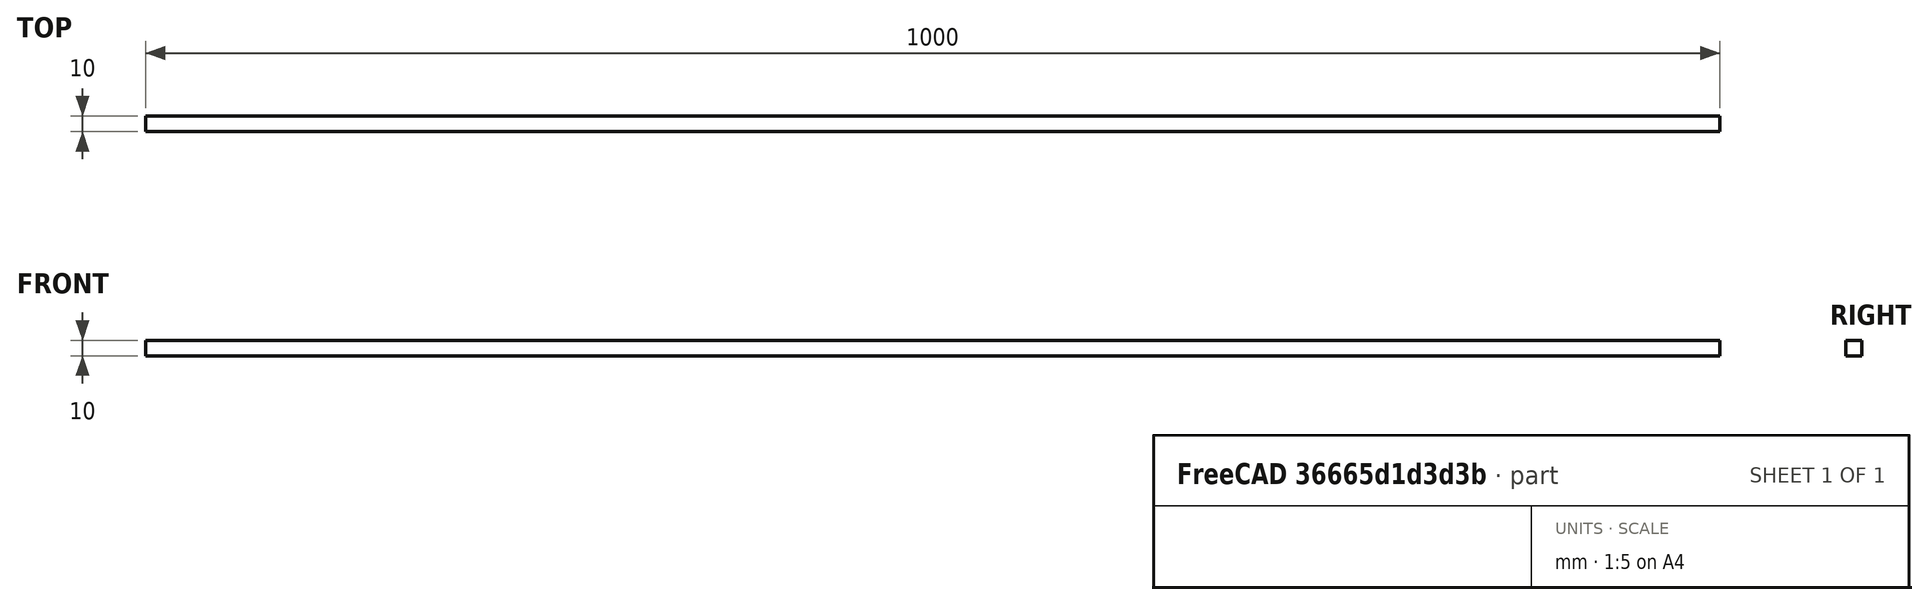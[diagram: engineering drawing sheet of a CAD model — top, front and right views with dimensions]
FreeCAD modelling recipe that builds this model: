
FCSTD DOCUMENT  (FreeCAD 0.21R33694 (Git))
Label: Elastica
License: All rights reserved
LicenseURL: http://en.wikipedia.org/wiki/All_rights_reserved
objects: Fem::FemMeshObjectPython×2, Part::Box×1, Fem::ConstraintForce×1, Fem::ConstraintFixed×1, App::MaterialObjectPython×1, Fem::FemSolverObjectPython×1, Fem::FemResultObjectPython×1, Fem::FemAnalysis×1
note: 1 computed B-rep shape members (.brp) not serialized (recipe doc carries the construction recipe, not evaluated geometry)

FEATURE [Part::Box] Box  label="Cube"
  AttacherType = Attacher::AttachEngine3D
  Height = 10
  Length = 1000
  MapMode = 0
  Width = 10
FEATURE [Fem::ConstraintForce] ConstraintForce
  Direction = -> Box [Edge5]
  DirectionVector = (0,0,-1)
  Force = 175
  NormalDirection = (1,0,0)
  References = -> [Box]
  Reversed = true
  Scale = 1
FEATURE [Fem::ConstraintFixed] ConstraintFixed
  NormalDirection = (-1,0,0)
  References = -> [Box]
  Scale = 1
FEATURE [App::MaterialObjectPython] MaterialSolid  # WARN: FeaturePython — macro-defined, semantics opaque (R4)
  Category = 0
FEATURE [Fem::FemMeshObjectPython] FEMMeshGmsh  # WARN: FeaturePython — macro-defined, semantics opaque (R4)
  Algorithm2D = 0
  Algorithm3D = 0
  CharacteristicLengthMax = 0
  CharacteristicLengthMin = 0
  CoherenceMesh = true
  ElementDimension = 0
  ElementOrder = 1
  GeometryTolerance = 1e-06
  GroupsOfNodes = false
  HighOrderOptimize = 0
  MeshSizeFromCurvature = 12
  OptimizeNetgen = false
  OptimizeStd = true
  Part = -> Box
  RecombinationAlgorithm = 0
  Recombine3DAll = false
  RecombineAll = false
  SecondOrderLinear = false
FEATURE [Fem::FemSolverObjectPython] SolverCcxTools  # WARN: FeaturePython — macro-defined, semantics opaque (R4)
  AnalysisType = 0
  BeamShellResultOutput3D = false
  BucklingFactors = 1
  EigenmodeHighLimit = 1000000
  EigenmodeLowLimit = 0
  EigenmodesCount = 10
  GeometricalNonlinearity = 0
  IterationsControlParameterCutb = 0.25,0.5,0.75,0.85,,,1.5,
  IterationsControlParameterIter = 4,8,9,200,10,400,,200,,
  IterationsControlParameterTimeUse = false
  IterationsThermoMechMaximum = 2000
  IterationsUserDefinedIncrementations = false
  IterationsUserDefinedTimeStepLength = false
  MaterialNonlinearity = 0
  MatrixSolverType = 0
  SplitInputWriter = false
  ThermoMechSteadyState = true
  TimeEnd = 1
  TimeInitialStep = 0.01
FEATURE [Fem::FemMeshObjectPython] Result_Mesh_Volume  # WARN: FeaturePython — macro-defined, semantics opaque (R4)
FEATURE [Fem::FemResultObjectPython] ResultMechanical  # WARN: FeaturePython — macro-defined, semantics opaque (R4)
  Eigenmode = 0
  EigenmodeFrequency = 0
  Mesh = -> Result_Mesh_Volume
  ResultType = Fem::ResultMechanical
  Time = 0
FEATURE [Fem::FemAnalysis] Analysis
  Group = -> [ConstraintForce,ConstraintFixed,MaterialSolid,FEMMeshGmsh,SolverCcxTools,ResultMechanical]
